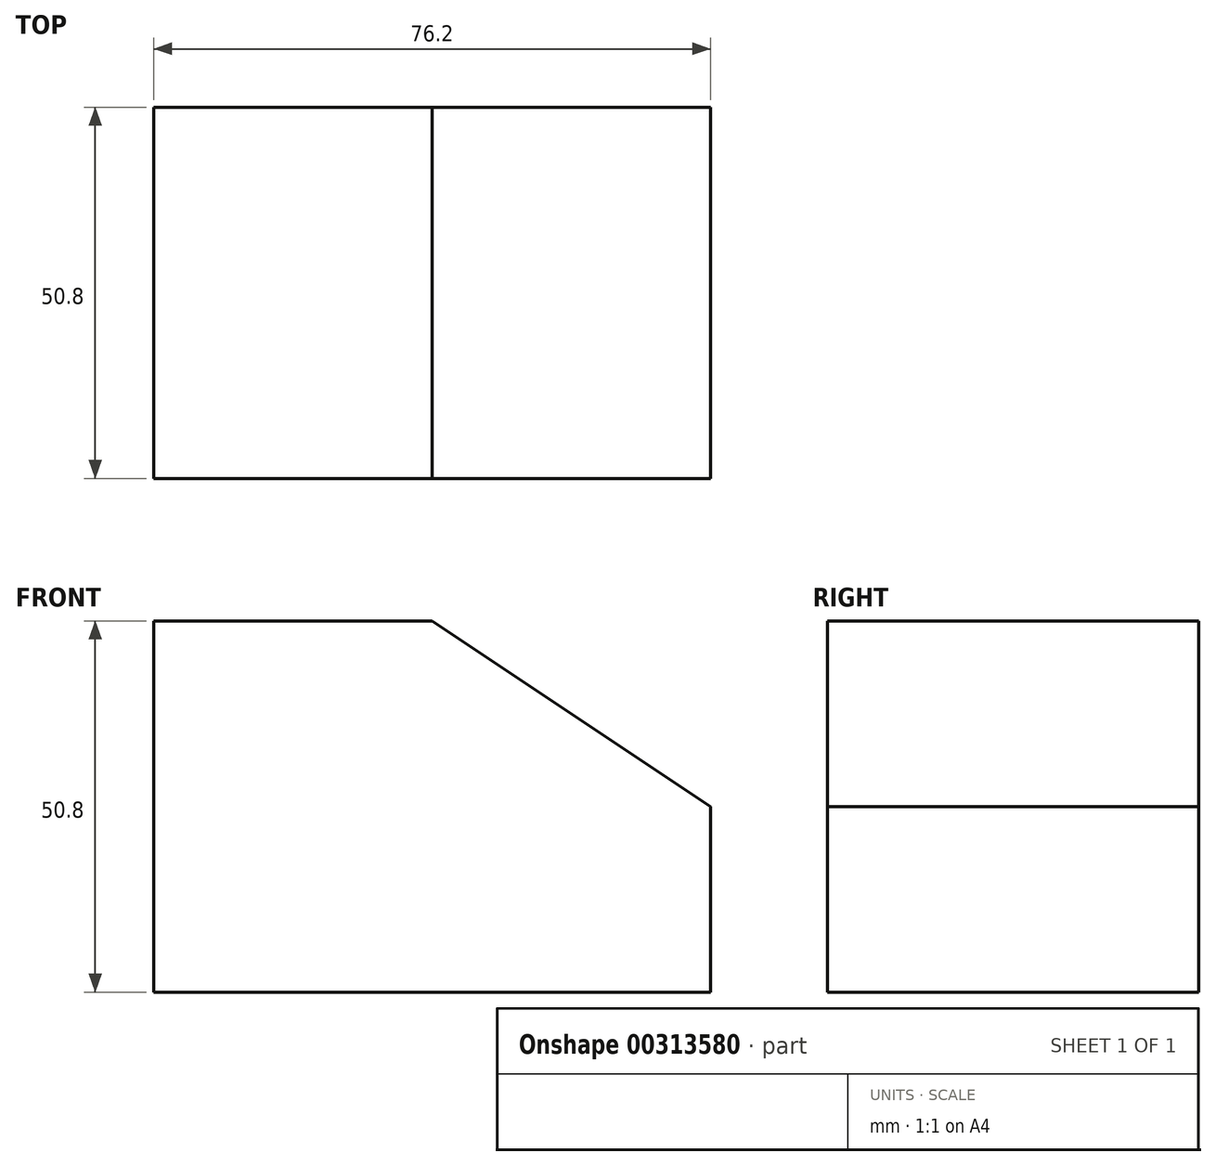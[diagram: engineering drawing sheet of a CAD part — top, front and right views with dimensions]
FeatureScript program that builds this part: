
annotation { "Feature Type Name" : "Feature", "Feature Type Description" : "" }
export const myFeature = defineFeature(function(context is Context, id is Id, definition is map)
    precondition{}
    {
        {
            var Q0;
            Q0=qCreatedBy(makeId("Front.planeOp"),FACE);
            var sketch = newSketch(context, id + "F0", { "sketchPlane" : qUnion([Q0])});
            skLineSegment(sketch, "E0", {"start": v(-27.74, -62.1) * mm, "end": v(48.46, -62.1) * mm});
            skLineSegment(sketch, "E1", {"start": v(48.46, -62.1) * mm, "end": v(48.46, -36.7) * mm});
            skLineSegment(sketch, "E2", {"start": v(48.46, -36.7) * mm, "end": v(10.36, -11.3) * mm});
            skLineSegment(sketch, "E3", {"start": v(10.36, -11.3) * mm, "end": v(-27.74, -11.3) * mm});
            skLineSegment(sketch, "E4", {"start": v(-27.74, -11.3) * mm, "end": v(-27.74, -62.1) * mm});
            skSolve(sketch);
        }
        {
            var Q0;
            Q0=makeQuery(id+"F0.imprint","IMPRINT",FACE,{"disambiguationData":[TD([[makeQuery(id+"F0.imprint","IMPRINT",EDGE,{"derivedFrom":sQuery(id+"F0.wireOp",EDGE,"E0")}),1.0]])]});
            extrude(context, id + "F1", {"entities" : qUnion([Q0]), "depth" : 50.8 * mm});
        }
    });
